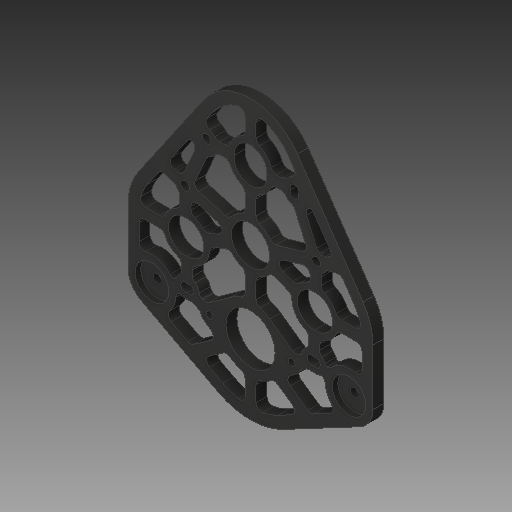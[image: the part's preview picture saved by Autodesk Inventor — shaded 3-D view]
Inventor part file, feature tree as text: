
AUTODESK INVENTOR PART (.ipt)
format: ipt  version: 2018 (Build 220112000, 112)  size: 412,672 bytes
history: native  units: in
note: dims shown in document units (in); Inventor stores cm internally (conversion verified against a paired STEP export)
features: fillet x1
ambient origin geometry x8: Origin, YZ Plane, XZ Plane, XY Plane, X Axis, Y Axis, Z Axis, Center Point
bodies: Solid1 (feature_tree)
feature tree (1):
  fillet  "Fillet68"  [1 undecoded]
note: 1 required parameter value undecoded (feature->parameter linkage not recoverable at this tier; creation-order binding heuristic only, values carry confidence <= 0.55)
